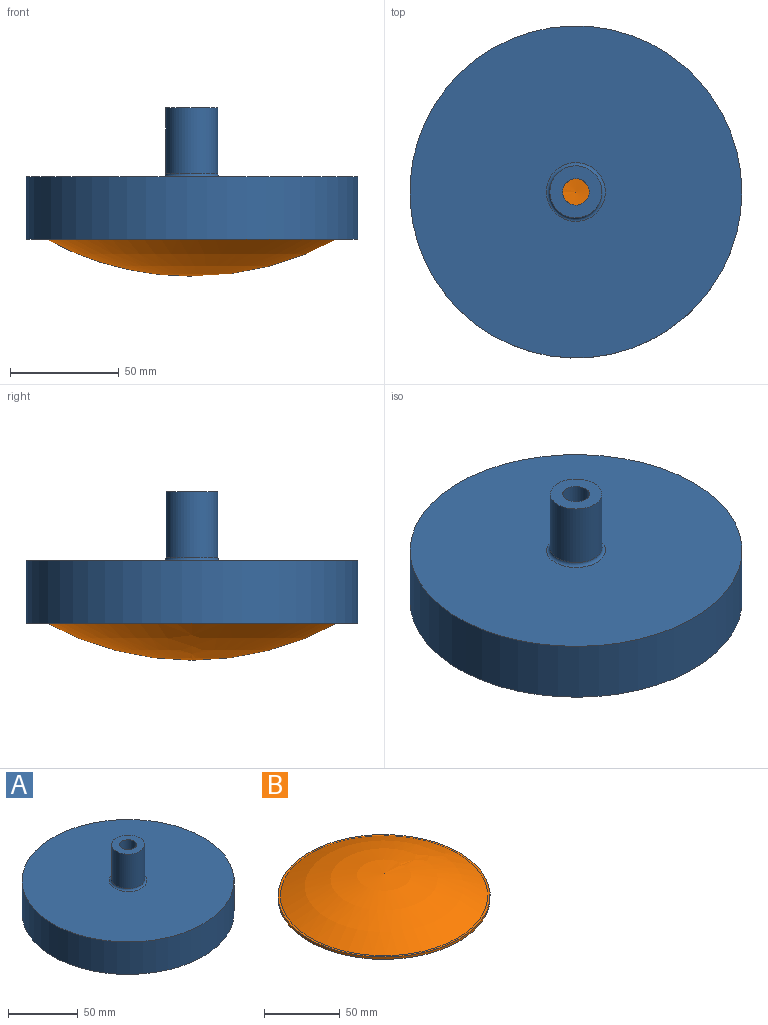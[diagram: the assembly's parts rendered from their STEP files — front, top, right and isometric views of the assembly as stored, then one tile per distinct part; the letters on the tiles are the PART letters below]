
ASSEMBLY  parts=2 mates=1
PART A: 13 faces, bbox 152.4x152.4x60.3 mm
  f0: cylinder r=6.1mm len=37.1mm, axis (0,0,1), area 1421mm2, adj f6,f12
  f1: cylinder r=67.95mm len=135.89mm, axis (0,0,-1), area 1463.9mm2, adj f8,f10
  f2: cylinder r=76.2mm len=152.4mm, axis (0,0,1), area 13681.1mm2, adj f3,f4
  f3: plane 152.4x152.4mm, normal (0,0,-1), area 2913.6mm2, adj f2,f9
  f4: plane 152.4x152.4mm, normal (0,0,1), area 17668.4mm2, adj f2,f7
  f5: cylinder r=11.91mm len=30.15mm, axis (0,0,-1), area 2255.5mm2, adj f6,f7
  f6: plane 23.81x23.81mm, normal (0,0,1), area 328.6mm2, adj f0,f5
  f7: torus R=13.51mm, axis (0,0,1), area 197.2mm2, adj f4,f5
  f8: plane 139.7x139.7mm, normal (0,0,-1), area 824.7mm2, adj f1,f9
  f9: cylinder r=69.85mm len=139.7mm, axis (0,0,-1), area 1215.1mm2, adj f3,f8
  f10: torus R=62.87mm, axis (0,0,-1), area 3314mm2, adj f1,f11
  f11: cone r=62.87mm half-angle=85deg, axis (0,0,-1), area 11925.8mm2, adj f10,f12
  f12: torus R=13.72mm, axis (0,0,-1), area 610.8mm2, adj f0,f11
PART B: 5 faces, bbox 139.7x139.7x19.8 mm
  f0: sphere r=139.7mm, area 10922mm2, adj f1
  f1: plane 139.7x139.7mm, normal (0,0,-1), area 4892.3mm2, adj f0,f2
  f2: cylinder r=69.85mm len=139.7mm, axis (0,0,1), area 836.1mm2, adj f1,f3
  f3: plane 139.7x139.7mm, normal (0,0,1), area 661.6mm2, adj f2,f4
  f4: sphere r=139.7mm, area 15667.2mm2, adj f3
PLACE A t=(-9.34,17.21,32.32)mm
PLACE B rot(axis=(0,1,0),180deg) t=(-9.34,17.21,6.51)mm
MATE fastened B.f2 <-> A.f9  axis (0,0,1) through (-9.34,17.21,6.51)mm
